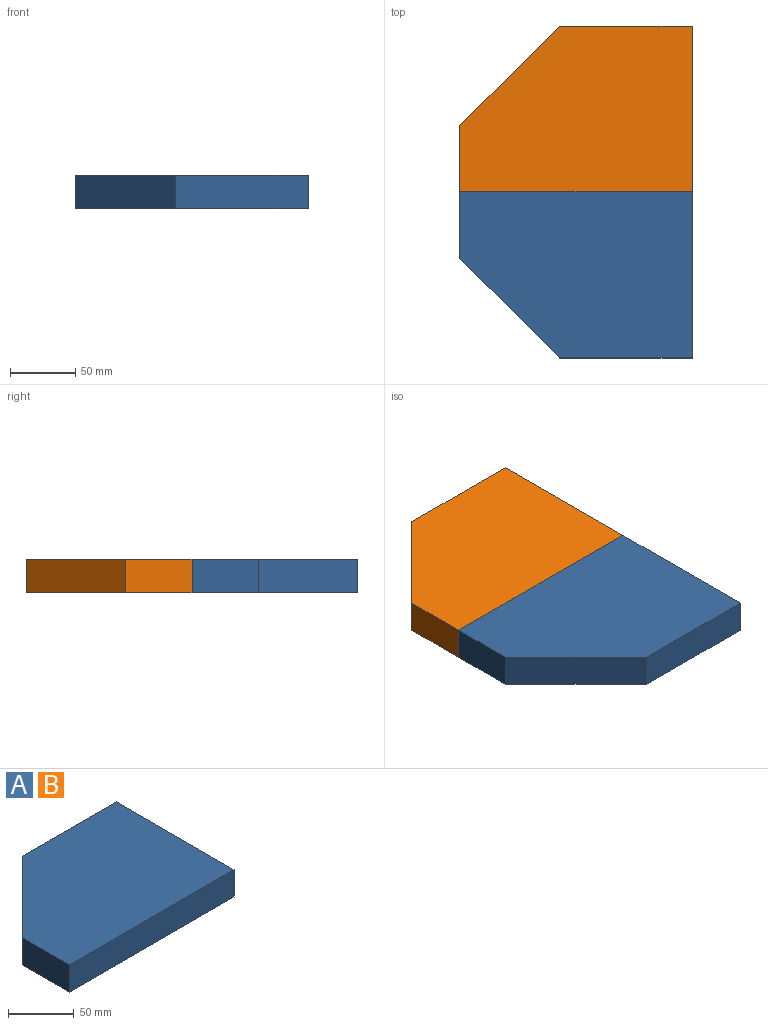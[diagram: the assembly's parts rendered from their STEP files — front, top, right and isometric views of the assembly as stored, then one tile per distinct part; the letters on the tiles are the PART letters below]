
ASSEMBLY  parts=2 mates=1
PART A: 7 faces, bbox 177.8x127x25.4 mm
  f0: plane 76.2x76.2mm, normal (-0.71,0.71,0), area 2737.2mm2, adj f1,f4,f5,f6
  f1: plane 50.8x25.4mm, normal (-1,0,0), area 1290.3mm2, adj f0,f2,f5,f6
  f2: plane 177.8x25.4mm, normal (0,-1,0), area 4516.1mm2, adj f1,f3,f5,f6
  f3: plane 127x25.4mm, normal (1,0,0), area 3225.8mm2, adj f2,f4,f5,f6
  f4: plane 101.6x25.4mm, normal (0,1,0), area 2580.6mm2, adj f0,f3,f5,f6
  f5: plane 177.8x127mm, normal (0,0,1), area 19677.4mm2, adj f0,f1,f2,f3,f4
  f6: plane 177.8x127mm, normal (0,0,-1), area 19677.4mm2, adj f0,f1,f2,f3,f4
PART B: same geometry as A
PLACE A rot(axis=(1,0,0),180deg) t=(-9.88,10.33,55.01)mm
PLACE B t=(-9.88,10.33,29.61)mm fixed
MATE fastened A.f6 <-> B.f5  axis (0,0,1) through (79.02,10.33,55.01)mm
